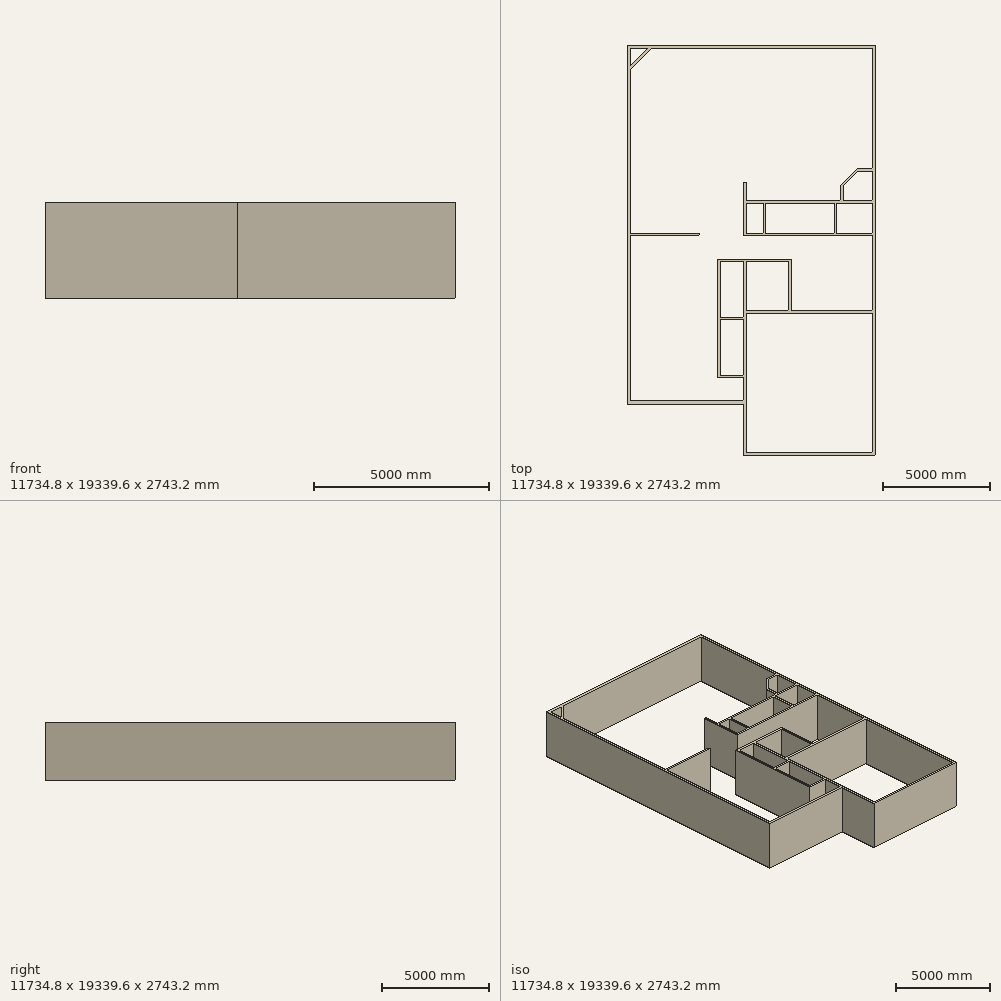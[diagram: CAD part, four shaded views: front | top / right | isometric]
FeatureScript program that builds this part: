
annotation { "Feature Type Name" : "Feature", "Feature Type Description" : "" }
export const myFeature = defineFeature(function(context is Context, id is Id, definition is map)
    precondition{}
    {
        {
            var Q0;
            Q0=qCreatedBy(makeId("Top.planeOp"),FACE);
            var sketch = newSketch(context, id + "F0", { "sketchPlane" : qUnion([Q0])});
            skLineSegment(sketch, "E0.bottom", {"start": v(-304.8, -8382) * mm, "end": v(-5791.2, -8382) * mm});
            skLineSegment(sketch, "E0.top", {"start": v(5791.2, 8382) * mm, "end": v(-5791.2, 8382) * mm});
            skLineSegment(sketch, "E0.left", {"start": v(5791.2, -10820.4) * mm, "end": v(5791.2, 8382) * mm});
            skLineSegment(sketch, "E0.right", {"start": v(-5791.2, -8382) * mm, "end": v(-5791.2, 8382) * mm});
            skPoint(sketch, "E0.middle", {"position": v(0, 0) * mm});
            skLineSegment(sketch, "E1", {"start": v(-304.8, -10820.4) * mm, "end": v(-304.8, -1676.4) * mm});
            skLineSegment(sketch, "E2", {"start": v(-304.8, -7162.8) * mm, "end": v(-1524, -7162.8) * mm});
            skLineSegment(sketch, "E3", {"start": v(-1524, -7162.8) * mm, "end": v(-1524, -1676.4) * mm});
            skLineSegment(sketch, "E4", {"start": v(-1524, -1676.4) * mm, "end": v(1828.8, -1676.4) * mm});
            skLineSegment(sketch, "E5", {"start": v(1828.8, -1676.4) * mm, "end": v(1828.8, -4114.8) * mm});
            skLineSegment(sketch, "E6", {"start": v(-304.8, -4114.8) * mm, "end": v(5791.2, -4114.8) * mm});
            skPoint(sketch, "E6.endSnap0", {"position": v(5791.2, 0) * mm});
            skLineSegment(sketch, "E7", {"start": v(-5791.2, -457.2) * mm, "end": v(-2438.4, -457.2) * mm});
            skLineSegment(sketch, "E8", {"start": v(-1524, -4419.6) * mm, "end": v(-304.8, -4419.6) * mm});
            skLineSegment(sketch, "E9", {"start": v(-304.8, 1981.2) * mm, "end": v(-304.8, -457.2) * mm});
            skLineSegment(sketch, "E10", {"start": v(-304.8, -457.2) * mm, "end": v(5791.2, -457.2) * mm});
            skLineSegment(sketch, "E11", {"start": v(3962.4, 1066.8) * mm, "end": v(3962.4, -457.2) * mm});
            skLineSegment(sketch, "E12", {"start": v(-304.8, 1066.8) * mm, "end": v(5791.2, 1066.8) * mm});
            skLineSegment(sketch, "E13", {"start": v(609.6, 1066.8) * mm, "end": v(609.6, -457.2) * mm});
            skLineSegment(sketch, "E14", {"start": v(-4713.57, 8382) * mm, "end": v(-5791.2, 7304.37) * mm});
            skLineSegment(sketch, "E15", {"start": v(4267.2, 1066.8) * mm, "end": v(4267.2, 1828.8) * mm});
            skLineSegment(sketch, "E16", {"start": v(4267.2, 1828.8) * mm, "end": v(5029.2, 2590.8) * mm});
            skLineSegment(sketch, "E17", {"start": v(5029.2, 2590.8) * mm, "end": v(5791.2, 2590.8) * mm});
            skLineSegment(sketch, "E18", {"start": v(-304.8, -10820.4) * mm, "end": v(5791.2, -10820.4) * mm});
            skPoint(sketch, "E19.orphan", {"position": v(5791.2, -8382) * mm});
            skSolve(sketch);
        }
        {
            var Q0;
            Q0=qCreatedBy(makeId("Top.planeOp"),FACE);
            var sketch = newSketch(context, id + "F1", { "sketchPlane" : qUnion([Q0])});
            skLineSegment(sketch, "E20.0", {"start": v(5867.4, -10881.36) * mm, "end": v(5867.4, 8458.2) * mm});
            skLineSegment(sketch, "E20.1", {"start": v(5867.4, 8458.2) * mm, "end": v(-5867.4, 8458.2) * mm});
            skLineSegment(sketch, "E20.2", {"start": v(-5867.4, -8458.2) * mm, "end": v(-5867.4, 8458.2) * mm});
            skLineSegment(sketch, "E20.3", {"start": v(-304.8, -8458.2) * mm, "end": v(-5867.4, -8458.2) * mm});
            skLineSegment(sketch, "E21.0", {"start": v(5715, -10820.4) * mm, "end": v(5715, 8305.8) * mm});
            skLineSegment(sketch, "E21.1", {"start": v(5715, 8305.8) * mm, "end": v(-5715, 8305.8) * mm});
            skLineSegment(sketch, "E21.2", {"start": v(-5715, -8305.8) * mm, "end": v(-5715, 8305.8) * mm});
            skLineSegment(sketch, "E21.3", {"start": v(-304.8, -8305.8) * mm, "end": v(-5715, -8305.8) * mm});
            skLineSegment(sketch, "E22.0", {"start": v(-4756.67, 8425.1) * mm, "end": v(-5834.3, 7347.47) * mm});
            skLineSegment(sketch, "E23.0", {"start": v(-4670.46, 8338.9) * mm, "end": v(-5748.1, 7261.26) * mm});
            skLineSegment(sketch, "E24.0", {"start": v(-228.6, -10820.4) * mm, "end": v(-228.6, -1676.4) * mm});
            skLineSegment(sketch, "E25.0", {"start": v(-381, -10881.36) * mm, "end": v(-381, -1676.4) * mm});
            skLineSegment(sketch, "E26.0", {"start": v(-304.8, -4191) * mm, "end": v(5791.2, -4191) * mm});
            skLineSegment(sketch, "E27.0", {"start": v(-304.8, -4038.6) * mm, "end": v(5791.2, -4038.6) * mm});
            skLineSegment(sketch, "E28.0", {"start": v(1767.84, -1737.36) * mm, "end": v(1767.84, -4114.8) * mm});
            skLineSegment(sketch, "E28.1", {"start": v(-1463.04, -1737.36) * mm, "end": v(1767.84, -1737.36) * mm});
            skLineSegment(sketch, "E28.2", {"start": v(-1463.04, -7101.84) * mm, "end": v(-1463.04, -1737.36) * mm});
            skLineSegment(sketch, "E28.3", {"start": v(-304.8, -7101.84) * mm, "end": v(-1463.04, -7101.84) * mm});
            skLineSegment(sketch, "E29.0", {"start": v(1889.76, -1615.44) * mm, "end": v(1889.76, -4114.8) * mm});
            skLineSegment(sketch, "E29.1", {"start": v(-1584.96, -1615.44) * mm, "end": v(1889.76, -1615.44) * mm});
            skLineSegment(sketch, "E29.2", {"start": v(-1584.96, -7223.76) * mm, "end": v(-1584.96, -1615.44) * mm});
            skLineSegment(sketch, "E29.3", {"start": v(-304.8, -7223.76) * mm, "end": v(-1584.96, -7223.76) * mm});
            skLineSegment(sketch, "E30.0", {"start": v(-1524, -4480.56) * mm, "end": v(-304.8, -4480.56) * mm});
            skLineSegment(sketch, "E31.0", {"start": v(-1524, -4358.64) * mm, "end": v(-304.8, -4358.64) * mm});
            skLineSegment(sketch, "E32.0", {"start": v(-381, -10881.36) * mm, "end": v(5867.4, -10881.36) * mm});
            skLineSegment(sketch, "E33.0", {"start": v(-304.8, -10759.44) * mm, "end": v(5791.2, -10759.44) * mm});
            skLineSegment(sketch, "E34.0", {"start": v(-5791.2, -518.16) * mm, "end": v(-2438.4, -518.16) * mm});
            skLineSegment(sketch, "E35.0", {"start": v(-5791.2, -396.24) * mm, "end": v(-2438.4, -396.24) * mm});
            skLineSegment(sketch, "E36.0", {"start": v(-365.76, -518.16) * mm, "end": v(5791.2, -518.16) * mm});
            skLineSegment(sketch, "E36.1", {"start": v(-365.76, 1981.2) * mm, "end": v(-365.76, -518.16) * mm});
            skLineSegment(sketch, "E37.0", {"start": v(-243.84, -396.24) * mm, "end": v(5791.2, -396.24) * mm});
            skLineSegment(sketch, "E37.1", {"start": v(-243.84, 1981.2) * mm, "end": v(-243.84, -396.24) * mm});
            skLineSegment(sketch, "E38.0", {"start": v(-304.8, 1005.84) * mm, "end": v(5791.2, 1005.84) * mm});
            skLineSegment(sketch, "E39.0", {"start": v(-304.8, 1127.76) * mm, "end": v(5791.2, 1127.76) * mm});
            skLineSegment(sketch, "E40.0", {"start": v(670.56, 1066.8) * mm, "end": v(670.56, -457.2) * mm});
            skLineSegment(sketch, "E41.0", {"start": v(548.64, 1066.8) * mm, "end": v(548.64, -457.2) * mm});
            skLineSegment(sketch, "E42.0", {"start": v(3901.44, 1066.8) * mm, "end": v(3901.44, -457.2) * mm});
            skLineSegment(sketch, "E43.0", {"start": v(4023.36, 1066.8) * mm, "end": v(4023.36, -457.2) * mm});
            skLineSegment(sketch, "E44.0", {"start": v(5054.45, 2529.84) * mm, "end": v(5791.2, 2529.84) * mm});
            skLineSegment(sketch, "E44.1", {"start": v(4328.16, 1803.55) * mm, "end": v(5054.45, 2529.84) * mm});
            skLineSegment(sketch, "E44.2", {"start": v(4328.16, 1066.8) * mm, "end": v(4328.16, 1803.55) * mm});
            skLineSegment(sketch, "E45.0", {"start": v(5003.95, 2651.76) * mm, "end": v(5791.2, 2651.76) * mm});
            skLineSegment(sketch, "E45.1", {"start": v(4206.24, 1854.05) * mm, "end": v(5003.95, 2651.76) * mm});
            skLineSegment(sketch, "E45.2", {"start": v(4206.24, 1066.8) * mm, "end": v(4206.24, 1854.05) * mm});
            skLineSegment(sketch, "E46", {"start": v(-2438.4, -396.24) * mm, "end": v(-2438.4, -518.16) * mm});
            skLineSegment(sketch, "E47", {"start": v(-365.76, 1981.2) * mm, "end": v(-243.84, 1981.2) * mm});
            skSolve(sketch);
        }
        {
            var Q0;
            Q0 = qSketchRegion(id + "F1", true);
            var Q1;
            {var subQ0=sQuery(id+"F1.wireOp",EDGE,"E38.0");var subQ7=sQuery(id+"F1.wireOp",EDGE,"E21.0");var subQ8=makeQuery(id+"F1.imprint","INTERSECT",VERTEX,{"derivedFrom":[subQ7,subQ0]});Q1=makeQuery(id+"F1.imprint","IMPRINT",FACE,{"disambiguationData":[TD([[makeQuery(id+"F1.imprint","IMPRINT",EDGE,{"disambiguationData":[TD([[subQ8,-1.0]])],"derivedFrom":subQ7}),1.0]])]});}
            var Q2;
            {var subQ0=sQuery(id+"F1.wireOp",EDGE,"E41.0");var subQ1=sQuery(id+"F1.wireOp",EDGE,"E37.0");var subQ2=makeQuery(id+"F1.imprint","INTERSECT",VERTEX,{"derivedFrom":[subQ1,subQ0]});Q2=makeQuery(id+"F1.imprint","IMPRINT",FACE,{"disambiguationData":[TD([[makeQuery(id+"F1.imprint","IMPRINT",EDGE,{"disambiguationData":[TD([[subQ2,-1.0]])],"derivedFrom":subQ1}),1.0]])]});}
            var Q3;
            {var subQ13=sQuery(id+"F1.wireOp",EDGE,"E36.1");Q3=makeQuery(id+"F1.imprint","IMPRINT",FACE,{"disambiguationData":[TD([[makeQuery(id+"F1.imprint","IMPRINT",EDGE,{"derivedFrom":subQ13}),1.0]])]});}
            var Q4;
            {var subQ4=sQuery(id+"F1.wireOp",EDGE,"E26.0");var subQ5=sQuery(id+"F1.wireOp",EDGE,"E21.0");var subQ6=makeQuery(id+"F1.imprint","INTERSECT",VERTEX,{"derivedFrom":[subQ5,subQ4]});Q4=makeQuery(id+"F1.imprint","IMPRINT",FACE,{"disambiguationData":[TD([[makeQuery(id+"F1.imprint","IMPRINT",EDGE,{"disambiguationData":[TD([[subQ6,-1.0]])],"derivedFrom":subQ5}),1.0]])]});}
            var Q5;
            {var subQ5=sQuery(id+"F1.wireOp",EDGE,"E46");Q5=makeQuery(id+"F1.imprint","IMPRINT",FACE,{"disambiguationData":[TD([[makeQuery(id+"F1.imprint","IMPRINT",EDGE,{"derivedFrom":subQ5}),-1.0]])]});}
            var Q6;
            {var subQ12=sQuery(id+"F1.wireOp",EDGE,"E29.1");Q6=makeQuery(id+"F1.imprint","IMPRINT",FACE,{"disambiguationData":[TD([[makeQuery(id+"F1.imprint","IMPRINT",EDGE,{"derivedFrom":subQ12}),-1.0]])]});}
            var Q7;
            {var subQ0=sQuery(id+"F1.wireOp",EDGE,"E42.0");var subQ1=sQuery(id+"F1.wireOp",EDGE,"E37.0");var subQ2=makeQuery(id+"F1.imprint","INTERSECT",VERTEX,{"derivedFrom":[subQ1,subQ0]});Q7=makeQuery(id+"F1.imprint","IMPRINT",FACE,{"disambiguationData":[TD([[makeQuery(id+"F1.imprint","IMPRINT",EDGE,{"disambiguationData":[TD([[subQ2,-1.0]])],"derivedFrom":subQ1}),1.0]])]});}
            var Q8;
            {var subQ0=sQuery(id+"F1.wireOp",EDGE,"E44.1");Q8=makeQuery(id+"F1.imprint","IMPRINT",FACE,{"disambiguationData":[TD([[makeQuery(id+"F1.imprint","IMPRINT",EDGE,{"derivedFrom":subQ0}),1.0]])]});}
            var Q9;
            {var subQ0=sQuery(id+"F1.wireOp",EDGE,"E30.0");var subQ1=sQuery(id+"F1.wireOp",EDGE,"E25.0");var subQ2=makeQuery(id+"F1.imprint","INTERSECT",VERTEX,{"derivedFrom":[subQ1,subQ0]});Q9=makeQuery(id+"F1.imprint","IMPRINT",FACE,{"disambiguationData":[TD([[makeQuery(id+"F1.imprint","IMPRINT",EDGE,{"disambiguationData":[TD([[subQ2,-1.0]])],"derivedFrom":subQ1}),1.0]])]});}
            var Q10;
            {var subQ0=sQuery(id+"F1.wireOp",EDGE,"E23.0");var subQ1=sQuery(id+"F1.wireOp",EDGE,"E21.1");var subQ2=makeQuery(id+"F1.imprint","INTERSECT",VERTEX,{"derivedFrom":[subQ1,subQ0]});Q10=makeQuery(id+"F1.imprint","IMPRINT",FACE,{"disambiguationData":[TD([[makeQuery(id+"F1.imprint","IMPRINT",EDGE,{"disambiguationData":[TD([[subQ2,-1.0]])],"derivedFrom":subQ1}),1.0]])]});}
            extrude(context, id + "F2", {"entities" : qUnion([Q0, Q1, Q2, Q3, Q4, Q5, Q6, Q7, Q8, Q9, Q10]), "depth" : 2743.2 * mm});
        }
    });
